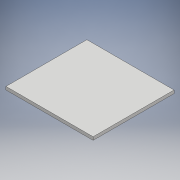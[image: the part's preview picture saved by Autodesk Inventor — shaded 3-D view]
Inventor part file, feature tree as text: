
AUTODESK INVENTOR PART (.ipt)
format: ipt  version: 2018 (Build 220112000, 112)  size: 90,112 bytes
history: native  units: mm
features: other x1, extrude x1, sketch x1
ambient origin geometry x8: Origin, YZ Plane, XZ Plane, XY Plane, X Axis, Y Axis, Z Axis, Center Point
bodies: Body1 (feature_tree)
feature tree (3):
  other  "Bryła1"
  extrude  "Wyciągnięcie proste1"  Depth=168.0mm
  sketch  "Szkic1"
